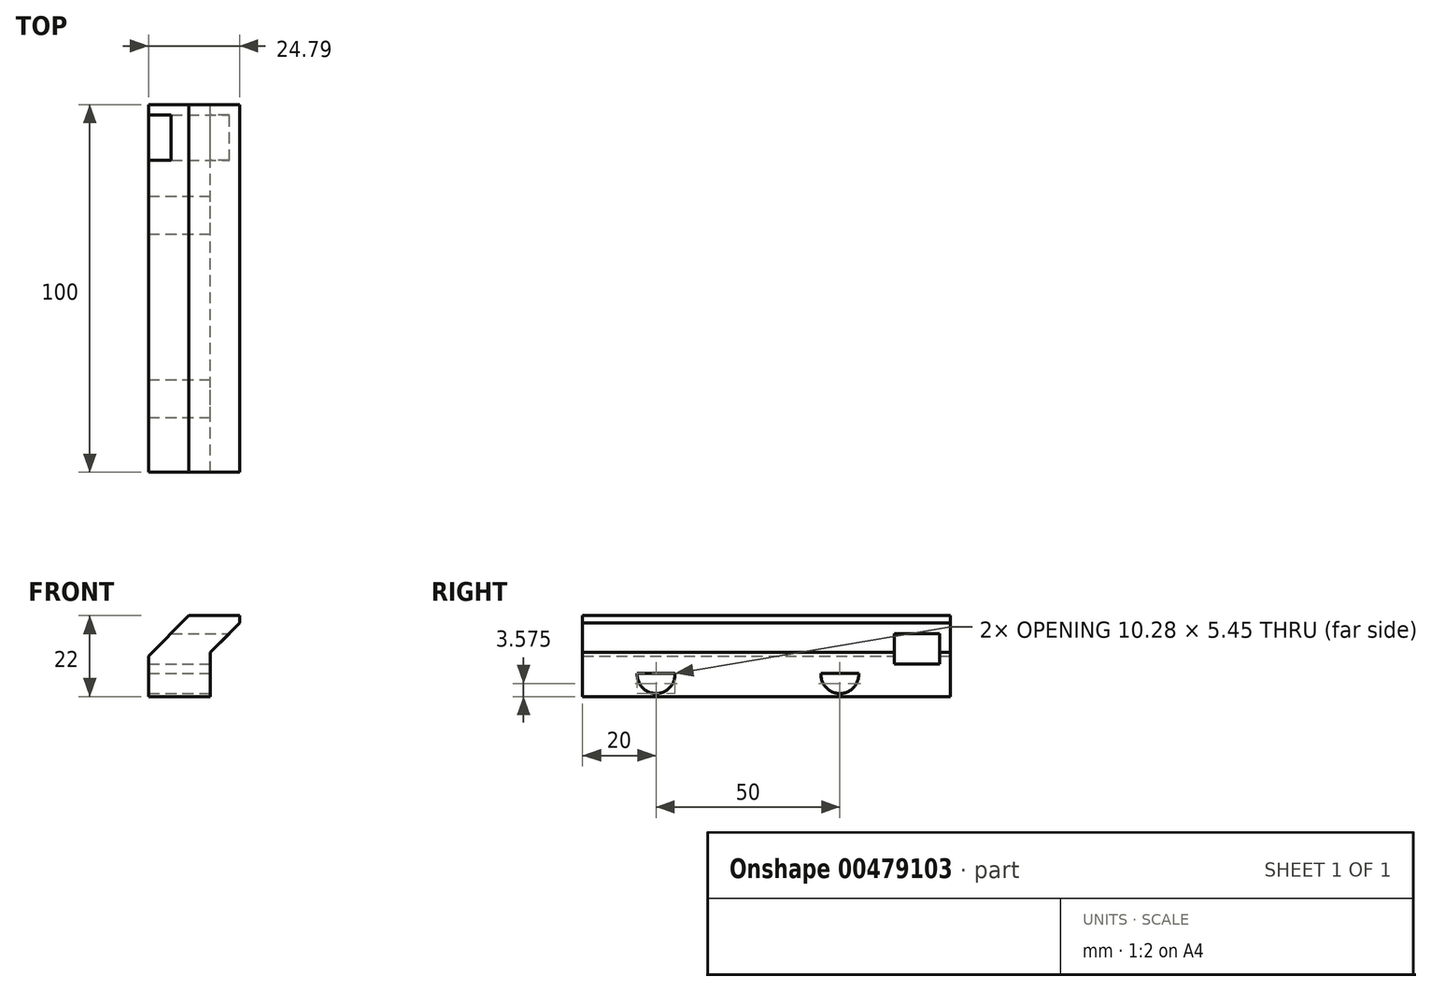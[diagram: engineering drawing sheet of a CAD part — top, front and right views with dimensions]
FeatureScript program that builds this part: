
annotation { "Feature Type Name" : "Feature", "Feature Type Description" : "" }
export const myFeature = defineFeature(function(context is Context, id is Id, definition is map)
    precondition{}
    {
        {
            var Q0;
            Q0=qCreatedBy(makeId("Front.planeOp"),FACE);
            var sketch = newSketch(context, id + "F0", { "sketchPlane" : qUnion([Q0])});
            skLineSegment(sketch, "E0", {"start": v(0, 0) * mm, "end": v(-16.79, 0) * mm});
            skLineSegment(sketch, "E1", {"start": v(-16.79, 0) * mm, "end": v(-16.79, 11) * mm});
            skLineSegment(sketch, "E2", {"start": v(-5.79, 22) * mm, "end": v(8, 22) * mm});
            skLineSegment(sketch, "E3", {"start": v(8, 20) * mm, "end": v(0, 12) * mm});
            skLineSegment(sketch, "E4", {"start": v(0, 12) * mm, "end": v(0, 0) * mm});
            skLineSegment(sketch, "E5", {"start": v(8, 20) * mm, "end": v(8, 22) * mm});
            skPoint(sketch, "E6.orphan", {"position": v(10, 22) * mm});
            skLineSegment(sketch, "E7", {"start": v(-16.79, 11) * mm, "end": v(-5.79, 22) * mm});
            skPoint(sketch, "E8.orphan", {"position": v(-16.79, 22) * mm});
            skSolve(sketch);
        }
        {
            var Q0;
            Q0=makeQuery(id+"F0.imprint","IMPRINT",FACE,{"disambiguationData":[TD([[makeQuery(id+"F0.imprint","IMPRINT",EDGE,{"derivedFrom":sQuery(id+"F0.wireOp",EDGE,"E0")}),-1.0]])]});
            extrude(context, id + "F1", {"entities" : qUnion([Q0]), "depth" : 100 * mm});
        }
        {
            var Q0;
            Q0=makeQuery(id+"F1.opExtrude","SWEPT_FACE",FACE,{"disambiguationData":[OSD([sQuery(id+"F0.wireOp",EDGE,"E4")])]});
            var sketch = newSketch(context, id + "F2", { "sketchPlane" : qUnion([Q0])});
            skPoint(sketch, "E9.centerSnap0", {"position": v(-100, 6) * mm});
            skPoint(sketch, "E10.centerSnap0", {"position": v(0, 6) * mm});
            skArc(sketch, "E11", {"start": v(-85.14, 6.3) * mm, "mid": v(-80, 0.85) * mm, "end": v(-74.86, 6.3) * mm});
            skArc(sketch, "E12", {"start": v(-35.14, 6.3) * mm, "mid": v(-30, 0.85) * mm, "end": v(-24.86, 6.3) * mm});
            skLineSegment(sketch, "E13", {"start": v(-85.14, 6.3) * mm, "end": v(-74.86, 6.3) * mm});
            skLineSegment(sketch, "E14.0", {"start": v(-35.15, 6.3) * mm, "end": v(-24.85, 6.3) * mm});
            skSolve(sketch);
        }
        {
            var Q0;
            Q0=makeQuery(id+"F2.imprint","IMPRINT",FACE,{"disambiguationData":[TD([[makeQuery(id+"F2.imprint","IMPRINT",EDGE,{"derivedFrom":sQuery(id+"F2.wireOp",EDGE,"E11")}),1.0]])]});
            var Q1;
            Q1=makeQuery(id+"F2.imprint","IMPRINT",FACE,{"disambiguationData":[TD([[makeQuery(id+"F2.imprint","IMPRINT",EDGE,{"derivedFrom":sQuery(id+"F2.wireOp",EDGE,"E12")}),1.0]])]});
            extrude(context, id + "F3", {"entities" : qUnion([Q0, Q1]), "operationType" : NewBodyOperationType.REMOVE, "oppositeDirection" : true, "depth" : 25 * mm});
        }
        {
            var Q0;
            Q0=makeQuery(id+"F1.opExtrude","SWEPT_FACE",FACE,{"disambiguationData":[OSD([sQuery(id+"F0.wireOp",EDGE,"E5")])]});
            var sketch = newSketch(context, id + "F4", { "sketchPlane" : qUnion([Q0])});
            skLineSegment(sketch, "E15.bottom", {"start": v(-15.15, 17.15) * mm, "end": v(-2.85, 17.15) * mm});
            skLineSegment(sketch, "E15.top", {"start": v(-15.15, 8.85) * mm, "end": v(-2.85, 8.85) * mm});
            skLineSegment(sketch, "E15.left", {"start": v(-15.15, 17.15) * mm, "end": v(-15.15, 8.85) * mm});
            skLineSegment(sketch, "E15.right", {"start": v(-2.85, 17.15) * mm, "end": v(-2.85, 8.85) * mm});
            skLineSegment(sketch, "E16", {"start": v(-9, 13) * mm, "end": v(-19.18, 13) * mm, "construction": true});
            skPoint(sketch, "E16.startSnap0", {"position": v(-2.85, 13) * mm});
            skPoint(sketch, "E16.startSnap1", {"position": v(-9, 8.85) * mm});
            skSolve(sketch);
        }
        {
            var Q0;
            Q0=makeQuery(id+"F4.imprint","IMPRINT",FACE,{"disambiguationData":[TD([[makeQuery(id+"F4.imprint","IMPRINT",EDGE,{"derivedFrom":sQuery(id+"F4.wireOp",EDGE,"E15.bottom")}),-1.0]])]});
            extrude(context, id + "F5", {"entities" : qUnion([Q0]), "operationType" : NewBodyOperationType.REMOVE, "oppositeDirection" : true, "depth" : 25 * mm});
        }
    });
